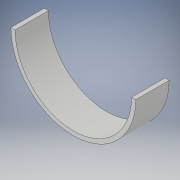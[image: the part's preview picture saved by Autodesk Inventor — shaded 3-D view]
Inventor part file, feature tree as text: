
AUTODESK INVENTOR PART (.ipt)
format: ipt  version: 2017 (Build 210142000, 142)  size: 103,936 bytes
history: native  units: in
note: dims shown in document units (in); Inventor stores cm internally (conversion verified against a paired STEP export)
features: sketch x2, sweep x1
ambient origin geometry x8: Origin, YZ Plane, XZ Plane, XY Plane, X Axis, Y Axis, Z Axis, Center Point
bodies: Solid1 (feature_tree)
feature tree (3):
  sweep  "Sweep1"
  sketch  "Sketch2"  dims[d0=0.5in d1=4.0in]
  sketch  "Sketch3"  dims[d2=0.5in d3=4.0in d6=0.0in d7=0.0in]
